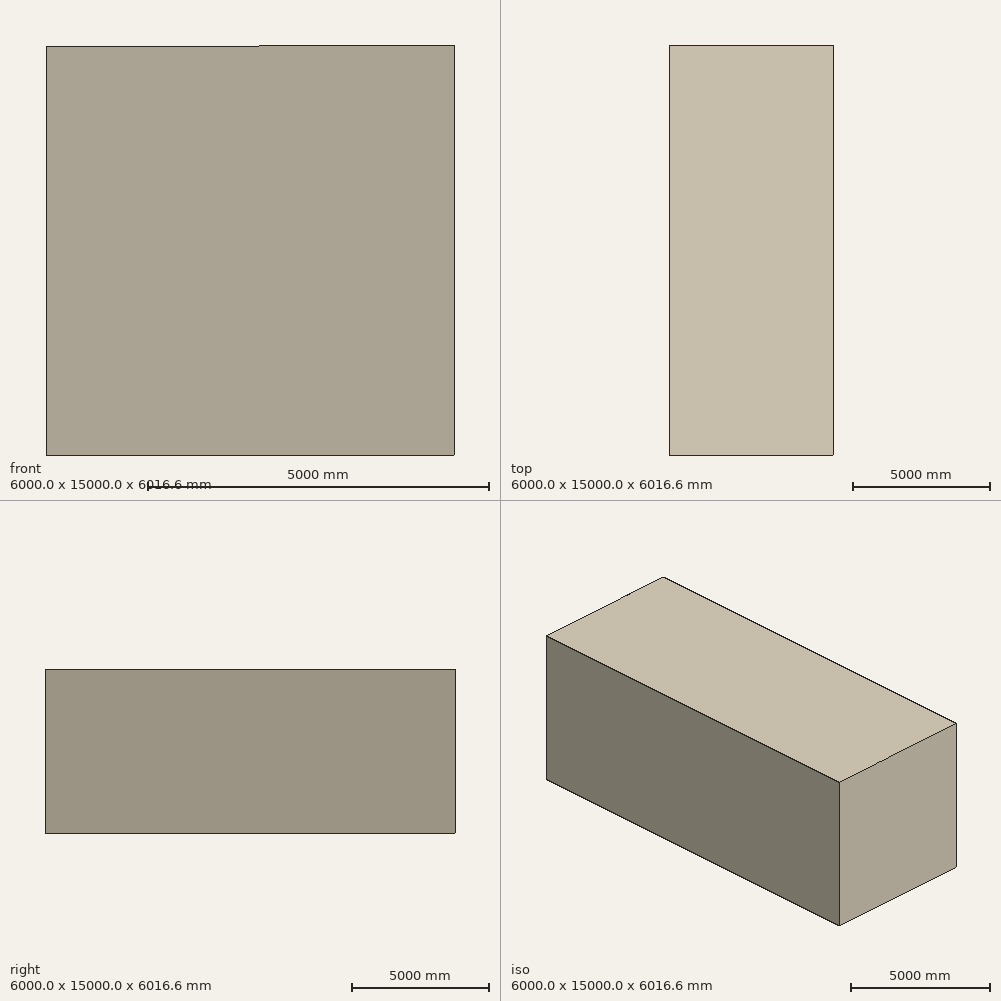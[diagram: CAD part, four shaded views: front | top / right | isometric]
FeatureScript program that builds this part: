
annotation { "Feature Type Name" : "Feature", "Feature Type Description" : "" }
export const myFeature = defineFeature(function(context is Context, id is Id, definition is map)
    precondition{}
    {
        {
            var Q0;
            Q0=qCreatedBy(makeId("Front.planeOp"),FACE);
            var sketch = newSketch(context, id + "F0", { "sketchPlane" : qUnion([Q0])});
            skLineSegment(sketch, "E0", {"start": v(-3012.05, 2582.05) * mm, "end": v(-3012.05, -3417.95) * mm});
            skLineSegment(sketch, "E1", {"start": v(-3012.05, -3417.95) * mm, "end": v(2987.95, -3417.95) * mm});
            skLineSegment(sketch, "E2", {"start": v(2987.95, -3417.95) * mm, "end": v(2987.95, 2598.62) * mm});
            skLineSegment(sketch, "E3", {"start": v(2987.95, 2598.62) * mm, "end": v(-3012.05, 2582.05) * mm});
            skSolve(sketch);
        }
        {
            var Q0;
            Q0 = qSketchRegion(id + "F0", true);
            extrude(context, id + "F1", {"entities" : qUnion([Q0]), "depth" : 15000 * mm});
        }
    });
